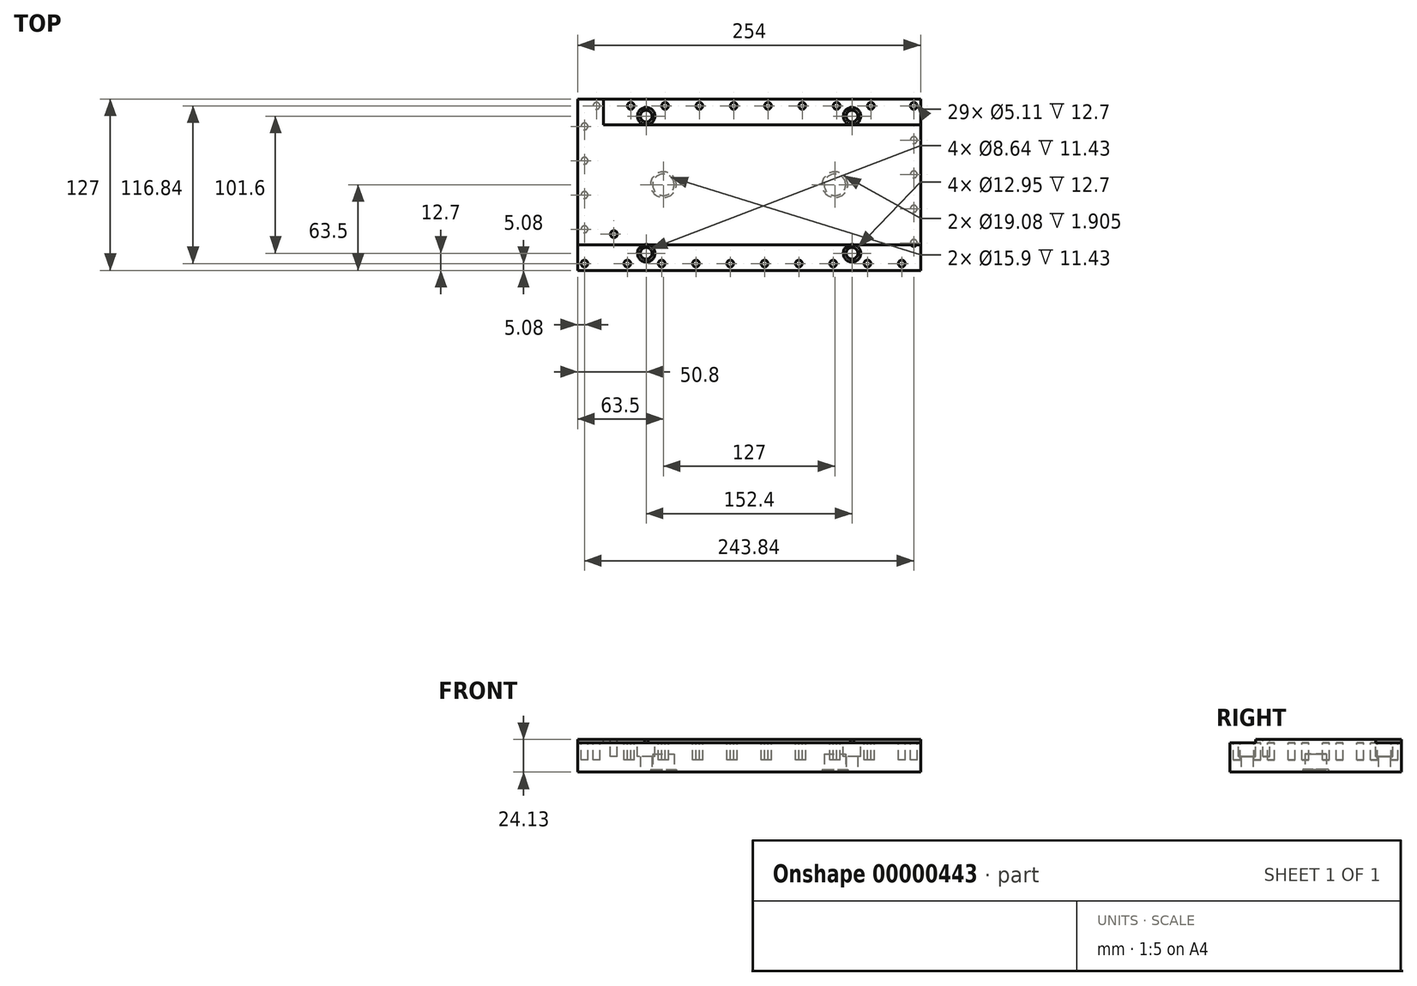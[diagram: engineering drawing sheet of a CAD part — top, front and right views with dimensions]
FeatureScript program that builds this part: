
annotation { "Feature Type Name" : "Feature", "Feature Type Description" : "" }
export const myFeature = defineFeature(function(context is Context, id is Id, definition is map)
    precondition{}
    {
        {
            var Q0;
            Q0=qCreatedBy(makeId("Top.planeOp"),FACE);
            var sketch = newSketch(context, id + "F0", { "sketchPlane" : qUnion([Q0])});
            skLineSegment(sketch, "E0.bottom", {"start": v(0, 0) * mm, "end": v(254, 0) * mm});
            skLineSegment(sketch, "E0.top", {"start": v(0, 127) * mm, "end": v(254, 127) * mm});
            skLineSegment(sketch, "E0.left", {"start": v(0, 0) * mm, "end": v(0, 127) * mm});
            skLineSegment(sketch, "E0.right", {"start": v(254, 0) * mm, "end": v(254, 127) * mm});
            skSolve(sketch);
        }
        {
            var Q0;
            Q0=makeQuery(id+"F0.imprint","IMPRINT",FACE,{"disambiguationData":[TD([[makeQuery(id+"F0.imprint","IMPRINT",EDGE,{"derivedFrom":sQuery(id+"F0.wireOp",EDGE,"E0.bottom")}),1.0]])]});
            extrude(context, id + "F1", {"entities" : qUnion([Q0]), "depth" : 24.13 * mm});
        }
        {
            var Q0;
            Q0=makeQuery(id+"F1.opExtrude","CAP_FACE",FACE,{"disambiguationData":[OSD([sQuery(id+"F0.wireOp",EDGE,"E0.bottom"),sQuery(id+"F0.wireOp",EDGE,"E0.top"),sQuery(id+"F0.wireOp",EDGE,"E0.left"),sQuery(id+"F0.wireOp",EDGE,"E0.right")])],"isStart":true});
            var sketch = newSketch(context, id + "F2", { "sketchPlane" : qUnion([Q0])});
            skCircle(sketch, "E1", {"center": v(190.5, -63.5) * mm, "radius": 7.95 * mm});
            skCircle(sketch, "E2", {"center": v(63.5, -63.5) * mm, "radius": 7.95 * mm});
            skSolve(sketch);
        }
        {
            var Q0;
            {Q0=qUnion([makeQuery(id+"F2.imprint","IMPRINT",FACE,{"disambiguationData":[TD([[makeQuery(id+"F2.imprint","IMPRINT",EDGE,{"derivedFrom":sQuery(id+"F2.wireOp",EDGE,"E1")}),1.0]])]}),makeQuery(id+"F2.imprint","IMPRINT",FACE,{"disambiguationData":[TD([[makeQuery(id+"F2.imprint","IMPRINT",EDGE,{"derivedFrom":sQuery(id+"F2.wireOp",EDGE,"E2")}),1.0]])]})]);}
            extrude(context, id + "F3", {"entities" : qUnion([Q0]), "operationType" : NewBodyOperationType.REMOVE, "oppositeDirection" : true, "depth" : 13.33 * mm});
        }
        {
            var Q0;
            Q0=makeQuery(id+"F1.opExtrude","CAP_FACE",FACE,{"disambiguationData":[OSD([sQuery(id+"F0.wireOp",EDGE,"E0.bottom"),sQuery(id+"F0.wireOp",EDGE,"E0.top"),sQuery(id+"F0.wireOp",EDGE,"E0.left"),sQuery(id+"F0.wireOp",EDGE,"E0.right")])],"isStart":true});
            var sketch = newSketch(context, id + "F4", { "sketchPlane" : qUnion([Q0])});
            skCircle(sketch, "E3", {"center": v(203.2, -114.3) * mm, "radius": 4.32 * mm});
            skCircle(sketch, "E4", {"center": v(203.2, -12.7) * mm, "radius": 4.32 * mm});
            skCircle(sketch, "E5", {"center": v(50.8, -114.3) * mm, "radius": 4.32 * mm});
            skCircle(sketch, "E6", {"center": v(50.8, -12.7) * mm, "radius": 4.32 * mm});
            skSolve(sketch);
        }
        {
            var Q0;
            {Q0=qUnion([makeQuery(id+"F4.imprint","IMPRINT",FACE,{"disambiguationData":[TD([[makeQuery(id+"F4.imprint","IMPRINT",EDGE,{"derivedFrom":sQuery(id+"F4.wireOp",EDGE,"E3")}),1.0]])]}),makeQuery(id+"F4.imprint","IMPRINT",FACE,{"disambiguationData":[TD([[makeQuery(id+"F4.imprint","IMPRINT",EDGE,{"derivedFrom":sQuery(id+"F4.wireOp",EDGE,"E4")}),1.0]])]}),makeQuery(id+"F4.imprint","IMPRINT",FACE,{"disambiguationData":[TD([[makeQuery(id+"F4.imprint","IMPRINT",EDGE,{"derivedFrom":sQuery(id+"F4.wireOp",EDGE,"E5")}),1.0]])]}),makeQuery(id+"F4.imprint","IMPRINT",FACE,{"disambiguationData":[TD([[makeQuery(id+"F4.imprint","IMPRINT",EDGE,{"derivedFrom":sQuery(id+"F4.wireOp",EDGE,"E6")}),1.0]])]})]);}
            extrude(context, id + "F5", {"entities" : qUnion([Q0]), "operationType" : NewBodyOperationType.REMOVE, "endBound" : BoundingType.THROUGH_ALL, "oppositeDirection" : true, "depth" : 25.4 * mm});
        }
        {
            var Q0;
            Q0=makeQuery(id+"F1.opExtrude","CAP_FACE",FACE,{"disambiguationData":[OSD([sQuery(id+"F0.wireOp",EDGE,"E0.bottom"),sQuery(id+"F0.wireOp",EDGE,"E0.top"),sQuery(id+"F0.wireOp",EDGE,"E0.left"),sQuery(id+"F0.wireOp",EDGE,"E0.right")])],"isStart":false});
            var sketch = newSketch(context, id + "F6", { "sketchPlane" : qUnion([Q0])});
            skCircle(sketch, "E7", {"center": v(50.8, 114.3) * mm, "radius": 6.48 * mm});
            skCircle(sketch, "E8", {"center": v(203.2, 114.3) * mm, "radius": 6.48 * mm});
            skCircle(sketch, "E9", {"center": v(50.8, 12.7) * mm, "radius": 6.48 * mm});
            skCircle(sketch, "E10", {"center": v(203.2, 12.7) * mm, "radius": 6.48 * mm});
            skSolve(sketch);
        }
        {
            var Q0;
            {var subQ0=makeQuery(id+"F1.opExtrude","CAP_FACE",FACE,{"disambiguationData":[OSD([sQuery(id+"F0.wireOp",EDGE,"E0.bottom"),sQuery(id+"F0.wireOp",EDGE,"E0.top"),sQuery(id+"F0.wireOp",EDGE,"E0.left"),sQuery(id+"F0.wireOp",EDGE,"E0.right")])],"isStart":false});var subQ1=makeQuery(id+"F6.imprint","IMPRINT",EDGE,{"derivedFrom":makeQuery(id+"F5.boolean.opBoolean","INTERSECT",EDGE,{"derivedFrom":[subQ0,makeQuery(id+"F5.opExtrude","SWEPT_FACE",FACE,{"disambiguationData":[OSD([sQuery(id+"F4.wireOp",EDGE,"E3")])]})]})});var subQ2=makeQuery(id+"F6.imprint","IMPRINT",EDGE,{"derivedFrom":makeQuery(id+"F5.boolean.opBoolean","INTERSECT",EDGE,{"derivedFrom":[subQ0,makeQuery(id+"F5.opExtrude","SWEPT_FACE",FACE,{"disambiguationData":[OSD([sQuery(id+"F4.wireOp",EDGE,"E4")])]})]})});var subQ3=makeQuery(id+"F6.imprint","IMPRINT",EDGE,{"derivedFrom":makeQuery(id+"F5.boolean.opBoolean","INTERSECT",EDGE,{"derivedFrom":[subQ0,makeQuery(id+"F5.opExtrude","SWEPT_FACE",FACE,{"disambiguationData":[OSD([sQuery(id+"F4.wireOp",EDGE,"E5")])]})]})});var subQ4=makeQuery(id+"F6.imprint","IMPRINT",EDGE,{"derivedFrom":makeQuery(id+"F5.boolean.opBoolean","INTERSECT",EDGE,{"derivedFrom":[subQ0,makeQuery(id+"F5.opExtrude","SWEPT_FACE",FACE,{"disambiguationData":[OSD([sQuery(id+"F4.wireOp",EDGE,"E6")])]})]})});Q0=qUnion([makeQuery(id+"F6.imprint","IMPRINT",FACE,{"disambiguationData":[TD([[subQ1,1.0]])]}),makeQuery(id+"F6.imprint","IMPRINT",FACE,{"disambiguationData":[TD([[subQ2,1.0]])]}),makeQuery(id+"F6.imprint","IMPRINT",FACE,{"disambiguationData":[TD([[subQ3,1.0]])]}),makeQuery(id+"F6.imprint","IMPRINT",FACE,{"disambiguationData":[TD([[subQ4,1.0]])]}),makeQuery(id+"F6.imprint","IMPRINT",FACE,{"disambiguationData":[TD([[makeQuery(id+"F6.imprint","IMPRINT",EDGE,{"derivedFrom":sQuery(id+"F6.wireOp",EDGE,"E7")}),1.0]])]}),makeQuery(id+"F6.imprint","IMPRINT",FACE,{"disambiguationData":[TD([[makeQuery(id+"F6.imprint","IMPRINT",EDGE,{"derivedFrom":sQuery(id+"F6.wireOp",EDGE,"E8")}),1.0]])]}),makeQuery(id+"F6.imprint","IMPRINT",FACE,{"disambiguationData":[TD([[makeQuery(id+"F6.imprint","IMPRINT",EDGE,{"derivedFrom":sQuery(id+"F6.wireOp",EDGE,"E9")}),1.0]])]}),makeQuery(id+"F6.imprint","IMPRINT",FACE,{"disambiguationData":[TD([[makeQuery(id+"F6.imprint","IMPRINT",EDGE,{"derivedFrom":sQuery(id+"F6.wireOp",EDGE,"E10")}),1.0]])]})]);}
            extrude(context, id + "F7", {"entities" : qUnion([Q0]), "operationType" : NewBodyOperationType.REMOVE, "oppositeDirection" : true, "depth" : 12.7 * mm});
        }
        {
            var Q0;
            Q0=makeQuery(id+"F1.opExtrude","CAP_FACE",FACE,{"disambiguationData":[OSD([sQuery(id+"F0.wireOp",EDGE,"E0.bottom"),sQuery(id+"F0.wireOp",EDGE,"E0.top"),sQuery(id+"F0.wireOp",EDGE,"E0.left"),sQuery(id+"F0.wireOp",EDGE,"E0.right")])],"isStart":false});
            var sketch = newSketch(context, id + "F8", { "sketchPlane" : qUnion([Q0])});
            skLineSegment(sketch, "E11.bottom", {"start": v(0, 19.05) * mm, "end": v(254, 19.05) * mm});
            skLineSegment(sketch, "E11.top", {"start": v(0, 0) * mm, "end": v(254, 0) * mm});
            skLineSegment(sketch, "E11.left", {"start": v(0, 19.05) * mm, "end": v(0, 0) * mm});
            skLineSegment(sketch, "E11.right", {"start": v(254, 19.05) * mm, "end": v(254, 0) * mm});
            skLineSegment(sketch, "E12.bottom", {"start": v(19.05, 19.05) * mm, "end": v(0, 19.05) * mm});
            skLineSegment(sketch, "E12.top", {"start": v(19.05, 127) * mm, "end": v(0, 127) * mm});
            skLineSegment(sketch, "E12.left", {"start": v(19.05, 19.05) * mm, "end": v(19.05, 127) * mm});
            skLineSegment(sketch, "E12.right", {"start": v(0, 19.05) * mm, "end": v(0, 127) * mm});
            skSolve(sketch);
        }
        {
            var Q0;
            {var subQ1=sQuery(id+"F8.wireOp",EDGE,"E12.bottom");var subQ2=makeQuery(id+"F8.imprint","IMPRINT",EDGE,{"derivedFrom":subQ1});var subQ3=makeQuery(id+"F7.boolean.opBoolean","COPY",EDGE,{"derivedFrom":makeQuery(id+"F7.opExtrude","CAP_EDGE",EDGE,{"disambiguationData":[OSD([sQuery(id+"F6.wireOp",EDGE,"E10")])],"isStart":true})});var subQ4=sQuery(id+"F8.wireOp",EDGE,"E11.bottom");var subQ6=makeQuery(id+"F8.imprint","INTERSECT",VERTEX,{"disambiguationData":[OD(0.0)],"derivedFrom":[subQ3,subQ4]});var subQ8=makeQuery(id+"F7.boolean.opBoolean","COPY",EDGE,{"derivedFrom":makeQuery(id+"F7.opExtrude","CAP_EDGE",EDGE,{"disambiguationData":[OSD([sQuery(id+"F6.wireOp",EDGE,"E9")])],"isStart":true})});var subQ10=makeQuery(id+"F8.imprint","INTERSECT",VERTEX,{"disambiguationData":[OD(0.0)],"derivedFrom":[subQ8,subQ4]});Q0=qUnion([makeQuery(id+"F8.imprint","IMPRINT",FACE,{"disambiguationData":[TD([[subQ2,-1.0]])]}),makeQuery(id+"F8.imprint","IMPRINT",FACE,{"disambiguationData":[TD([[makeQuery(id+"F8.imprint","IMPRINT",EDGE,{"derivedFrom":sQuery(id+"F8.wireOp",EDGE,"E11.top")}),1.0]])]}),makeQuery(id+"F8.imprint","IMPRINT",FACE,{"disambiguationData":[TD([[makeQuery(id+"F8.imprint","IMPRINT",EDGE,{"disambiguationData":[TD([[subQ10,-1.0]])],"derivedFrom":subQ4}),-1.0]])]}),makeQuery(id+"F8.imprint","IMPRINT",FACE,{"disambiguationData":[TD([[makeQuery(id+"F8.imprint","IMPRINT",EDGE,{"disambiguationData":[TD([[subQ6,-1.0]])],"derivedFrom":subQ4}),-1.0]])]})]);}
            extrude(context, id + "F9", {"entities" : qUnion([Q0]), "operationType" : NewBodyOperationType.REMOVE, "oppositeDirection" : true, "depth" : 2.54 * mm});
        }
        {
            var Q0;
            Q0=makeQuery(id+"F9.boolean.opBoolean","COPY",FACE,{"derivedFrom":makeQuery(id+"F9.opExtrude","CAP_FACE",FACE,{"disambiguationData":[OSD([sQuery(id+"F8.wireOp",EDGE,"E11.bottom"),sQuery(id+"F8.wireOp",EDGE,"E11.top"),sQuery(id+"F8.wireOp",EDGE,"E11.left"),sQuery(id+"F8.wireOp",EDGE,"E11.right"),sQuery(id+"F8.wireOp",EDGE,"E12.top"),sQuery(id+"F8.wireOp",EDGE,"E12.left"),sQuery(id+"F8.wireOp",EDGE,"E12.right")])],"isStart":false})});
            var sketch = newSketch(context, id + "F10", { "sketchPlane" : qUnion([Q0])});
            skCircle(sketch, "E13", {"center": v(5.08, 5.08) * mm, "radius": 2.55 * mm});
            skCircle(sketch, "E14", {"center": v(5.08, 30.48) * mm, "radius": 2.55 * mm});
            skCircle(sketch, "E15", {"center": v(5.08, 55.88) * mm, "radius": 2.55 * mm});
            skCircle(sketch, "E16", {"center": v(5.08, 81.28) * mm, "radius": 2.55 * mm});
            skCircle(sketch, "E17", {"center": v(36.83, 5.08) * mm, "radius": 2.55 * mm});
            skCircle(sketch, "E18", {"center": v(62.23, 5.08) * mm, "radius": 2.55 * mm});
            skCircle(sketch, "E19", {"center": v(87.63, 5.08) * mm, "radius": 2.55 * mm});
            skCircle(sketch, "E20", {"center": v(113.03, 5.08) * mm, "radius": 2.55 * mm});
            skCircle(sketch, "E21", {"center": v(138.43, 5.08) * mm, "radius": 2.55 * mm});
            skCircle(sketch, "E22", {"center": v(163.83, 5.08) * mm, "radius": 2.55 * mm});
            skCircle(sketch, "E23", {"center": v(189.23, 5.08) * mm, "radius": 2.55 * mm});
            skCircle(sketch, "E24", {"center": v(214.63, 5.08) * mm, "radius": 2.55 * mm});
            skCircle(sketch, "E25", {"center": v(5.08, 106.68) * mm, "radius": 2.55 * mm});
            skCircle(sketch, "E26", {"center": v(240.03, 5.08) * mm, "radius": 2.55 * mm});
            skSolve(sketch);
        }
        {
            var Q0;
            {Q0=qUnion([makeQuery(id+"F10.imprint","IMPRINT",FACE,{"disambiguationData":[TD([[makeQuery(id+"F10.imprint","IMPRINT",EDGE,{"derivedFrom":sQuery(id+"F10.wireOp",EDGE,"E13")}),1.0]])]}),makeQuery(id+"F10.imprint","IMPRINT",FACE,{"disambiguationData":[TD([[makeQuery(id+"F10.imprint","IMPRINT",EDGE,{"derivedFrom":sQuery(id+"F10.wireOp",EDGE,"E14")}),1.0]])]}),makeQuery(id+"F10.imprint","IMPRINT",FACE,{"disambiguationData":[TD([[makeQuery(id+"F10.imprint","IMPRINT",EDGE,{"derivedFrom":sQuery(id+"F10.wireOp",EDGE,"E15")}),1.0]])]}),makeQuery(id+"F10.imprint","IMPRINT",FACE,{"disambiguationData":[TD([[makeQuery(id+"F10.imprint","IMPRINT",EDGE,{"derivedFrom":sQuery(id+"F10.wireOp",EDGE,"E16")}),1.0]])]}),makeQuery(id+"F10.imprint","IMPRINT",FACE,{"disambiguationData":[TD([[makeQuery(id+"F10.imprint","IMPRINT",EDGE,{"derivedFrom":sQuery(id+"F10.wireOp",EDGE,"E17")}),1.0]])]}),makeQuery(id+"F10.imprint","IMPRINT",FACE,{"disambiguationData":[TD([[makeQuery(id+"F10.imprint","IMPRINT",EDGE,{"derivedFrom":sQuery(id+"F10.wireOp",EDGE,"E18")}),1.0]])]}),makeQuery(id+"F10.imprint","IMPRINT",FACE,{"disambiguationData":[TD([[makeQuery(id+"F10.imprint","IMPRINT",EDGE,{"derivedFrom":sQuery(id+"F10.wireOp",EDGE,"E19")}),1.0]])]}),makeQuery(id+"F10.imprint","IMPRINT",FACE,{"disambiguationData":[TD([[makeQuery(id+"F10.imprint","IMPRINT",EDGE,{"derivedFrom":sQuery(id+"F10.wireOp",EDGE,"E20")}),1.0]])]}),makeQuery(id+"F10.imprint","IMPRINT",FACE,{"disambiguationData":[TD([[makeQuery(id+"F10.imprint","IMPRINT",EDGE,{"derivedFrom":sQuery(id+"F10.wireOp",EDGE,"E21")}),1.0]])]}),makeQuery(id+"F10.imprint","IMPRINT",FACE,{"disambiguationData":[TD([[makeQuery(id+"F10.imprint","IMPRINT",EDGE,{"derivedFrom":sQuery(id+"F10.wireOp",EDGE,"E22")}),1.0]])]}),makeQuery(id+"F10.imprint","IMPRINT",FACE,{"disambiguationData":[TD([[makeQuery(id+"F10.imprint","IMPRINT",EDGE,{"derivedFrom":sQuery(id+"F10.wireOp",EDGE,"E23")}),1.0]])]}),makeQuery(id+"F10.imprint","IMPRINT",FACE,{"disambiguationData":[TD([[makeQuery(id+"F10.imprint","IMPRINT",EDGE,{"derivedFrom":sQuery(id+"F10.wireOp",EDGE,"E24")}),1.0]])]}),makeQuery(id+"F10.imprint","IMPRINT",FACE,{"disambiguationData":[TD([[makeQuery(id+"F10.imprint","IMPRINT",EDGE,{"derivedFrom":sQuery(id+"F10.wireOp",EDGE,"E25")}),1.0]])]}),makeQuery(id+"F10.imprint","IMPRINT",FACE,{"disambiguationData":[TD([[makeQuery(id+"F10.imprint","IMPRINT",EDGE,{"derivedFrom":sQuery(id+"F10.wireOp",EDGE,"E26")}),1.0]])]})]);}
            extrude(context, id + "F11", {"entities" : qUnion([Q0]), "operationType" : NewBodyOperationType.REMOVE, "oppositeDirection" : true, "depth" : 12.7 * mm});
        }
        {
            var Q0;
            Q0=makeQuery(id+"F1.opExtrude","CAP_FACE",FACE,{"disambiguationData":[OSD([sQuery(id+"F0.wireOp",EDGE,"E0.bottom"),sQuery(id+"F0.wireOp",EDGE,"E0.top"),sQuery(id+"F0.wireOp",EDGE,"E0.left"),sQuery(id+"F0.wireOp",EDGE,"E0.right")])],"isStart":false});
            var sketch = newSketch(context, id + "F12", { "sketchPlane" : qUnion([Q0])});
            skCircle(sketch, "E27", {"center": v(26.87, 26.87) * mm, "radius": 2.55 * mm});
            skSolve(sketch);
        }
        {
            var Q0;
            Q0=makeQuery(id+"F12.imprint","IMPRINT",FACE,{"disambiguationData":[TD([[makeQuery(id+"F12.imprint","IMPRINT",EDGE,{"derivedFrom":sQuery(id+"F12.wireOp",EDGE,"E27")}),1.0]])]});
            extrude(context, id + "F13", {"entities" : qUnion([Q0]), "operationType" : NewBodyOperationType.REMOVE, "oppositeDirection" : true, "depth" : 12.7 * mm});
        }
        {
            var Q0;
            Q0=makeQuery(id+"F1.opExtrude","CAP_FACE",FACE,{"disambiguationData":[OSD([sQuery(id+"F0.wireOp",EDGE,"E0.bottom"),sQuery(id+"F0.wireOp",EDGE,"E0.top"),sQuery(id+"F0.wireOp",EDGE,"E0.left"),sQuery(id+"F0.wireOp",EDGE,"E0.right")])],"isStart":false});
            var sketch = newSketch(context, id + "F14", { "sketchPlane" : qUnion([Q0])});
            skLineSegment(sketch, "E28.bottom", {"start": v(19.05, 127) * mm, "end": v(254, 127) * mm});
            skLineSegment(sketch, "E28.top", {"start": v(19.05, 107.95) * mm, "end": v(254, 107.95) * mm});
            skLineSegment(sketch, "E28.left", {"start": v(19.05, 127) * mm, "end": v(19.05, 107.95) * mm});
            skLineSegment(sketch, "E28.right", {"start": v(254, 127) * mm, "end": v(254, 107.95) * mm});
            skLineSegment(sketch, "E29.bottom", {"start": v(234.95, 107.95) * mm, "end": v(254, 107.95) * mm});
            skLineSegment(sketch, "E29.top", {"start": v(234.95, 19.05) * mm, "end": v(254, 19.05) * mm});
            skLineSegment(sketch, "E29.left", {"start": v(234.95, 107.95) * mm, "end": v(234.95, 19.05) * mm});
            skLineSegment(sketch, "E29.right", {"start": v(254, 107.95) * mm, "end": v(254, 19.05) * mm});
            skSolve(sketch);
        }
        {
            var Q0;
            {var subQ1=sQuery(id+"F14.wireOp",EDGE,"E29.bottom");var subQ2=makeQuery(id+"F14.imprint","IMPRINT",EDGE,{"derivedFrom":subQ1});var subQ3=makeQuery(id+"F7.boolean.opBoolean","COPY",EDGE,{"derivedFrom":makeQuery(id+"F7.opExtrude","CAP_EDGE",EDGE,{"disambiguationData":[OSD([sQuery(id+"F6.wireOp",EDGE,"E7")])],"isStart":true})});var subQ4=sQuery(id+"F14.wireOp",EDGE,"E28.top");var subQ6=makeQuery(id+"F14.imprint","INTERSECT",VERTEX,{"disambiguationData":[OD(0.0)],"derivedFrom":[subQ3,subQ4]});var subQ8=makeQuery(id+"F7.boolean.opBoolean","COPY",EDGE,{"derivedFrom":makeQuery(id+"F7.opExtrude","CAP_EDGE",EDGE,{"disambiguationData":[OSD([sQuery(id+"F6.wireOp",EDGE,"E8")])],"isStart":true})});var subQ10=makeQuery(id+"F14.imprint","INTERSECT",VERTEX,{"disambiguationData":[OD(0.0)],"derivedFrom":[subQ8,subQ4]});Q0=qUnion([makeQuery(id+"F14.imprint","IMPRINT",FACE,{"disambiguationData":[TD([[subQ2,-1.0]])]}),makeQuery(id+"F14.imprint","IMPRINT",FACE,{"disambiguationData":[TD([[makeQuery(id+"F14.imprint","IMPRINT",EDGE,{"derivedFrom":sQuery(id+"F14.wireOp",EDGE,"E28.bottom")}),-1.0]])]}),makeQuery(id+"F14.imprint","IMPRINT",FACE,{"disambiguationData":[TD([[makeQuery(id+"F14.imprint","IMPRINT",EDGE,{"disambiguationData":[TD([[subQ6,-1.0]])],"derivedFrom":subQ4}),1.0]])]}),makeQuery(id+"F14.imprint","IMPRINT",FACE,{"disambiguationData":[TD([[makeQuery(id+"F14.imprint","IMPRINT",EDGE,{"disambiguationData":[TD([[subQ10,-1.0]])],"derivedFrom":subQ4}),1.0]])]})]);}
            extrude(context, id + "F15", {"entities" : qUnion([Q0]), "operationType" : NewBodyOperationType.REMOVE, "oppositeDirection" : true, "depth" : 2.54 * mm});
        }
        {
            var Q0;
            Q0=makeQuery(id+"F15.boolean.opBoolean","MERGE",FACE,{"derivedFrom":[makeQuery(id+"F9.boolean.opBoolean","COPY",FACE,{"derivedFrom":makeQuery(id+"F9.opExtrude","CAP_FACE",FACE,{"disambiguationData":[OSD([sQuery(id+"F8.wireOp",EDGE,"E11.bottom"),sQuery(id+"F8.wireOp",EDGE,"E11.top"),sQuery(id+"F8.wireOp",EDGE,"E11.left"),sQuery(id+"F8.wireOp",EDGE,"E11.right"),sQuery(id+"F8.wireOp",EDGE,"E12.top"),sQuery(id+"F8.wireOp",EDGE,"E12.left"),sQuery(id+"F8.wireOp",EDGE,"E12.right")])],"isStart":false})}),makeQuery(id+"F15.opExtrude","CAP_FACE",FACE,{"disambiguationData":[OSD([sQuery(id+"F14.wireOp",EDGE,"E28.bottom"),sQuery(id+"F14.wireOp",EDGE,"E28.top"),sQuery(id+"F14.wireOp",EDGE,"E28.left"),sQuery(id+"F14.wireOp",EDGE,"E28.right"),sQuery(id+"F14.wireOp",EDGE,"E29.top"),sQuery(id+"F14.wireOp",EDGE,"E29.left"),sQuery(id+"F14.wireOp",EDGE,"E29.right")])],"isStart":false})]});
            var sketch = newSketch(context, id + "F16", { "sketchPlane" : qUnion([Q0])});
            skCircle(sketch, "E30", {"center": v(13.97, 121.92) * mm, "radius": 2.55 * mm});
            skCircle(sketch, "E31", {"center": v(39.37, 121.92) * mm, "radius": 2.55 * mm});
            skCircle(sketch, "E32", {"center": v(64.77, 121.92) * mm, "radius": 2.55 * mm});
            skCircle(sketch, "E33", {"center": v(90.17, 121.92) * mm, "radius": 2.55 * mm});
            skCircle(sketch, "E34", {"center": v(115.57, 121.92) * mm, "radius": 2.55 * mm});
            skCircle(sketch, "E35", {"center": v(140.97, 121.92) * mm, "radius": 2.55 * mm});
            skCircle(sketch, "E36", {"center": v(166.37, 121.92) * mm, "radius": 2.55 * mm});
            skCircle(sketch, "E37", {"center": v(191.77, 121.92) * mm, "radius": 2.55 * mm});
            skCircle(sketch, "E38", {"center": v(217.17, 121.92) * mm, "radius": 2.55 * mm});
            skCircle(sketch, "E39", {"center": v(248.92, 20.32) * mm, "radius": 2.55 * mm});
            skCircle(sketch, "E40", {"center": v(248.92, 45.72) * mm, "radius": 2.55 * mm});
            skCircle(sketch, "E41", {"center": v(248.92, 71.12) * mm, "radius": 2.55 * mm});
            skCircle(sketch, "E42", {"center": v(248.92, 96.52) * mm, "radius": 2.55 * mm});
            skCircle(sketch, "E43", {"center": v(248.92, 121.92) * mm, "radius": 2.55 * mm});
            skSolve(sketch);
        }
        {
            var Q0;
            {Q0=qUnion([makeQuery(id+"F16.imprint","IMPRINT",FACE,{"disambiguationData":[TD([[makeQuery(id+"F16.imprint","IMPRINT",EDGE,{"derivedFrom":sQuery(id+"F16.wireOp",EDGE,"E30")}),1.0]])]}),makeQuery(id+"F16.imprint","IMPRINT",FACE,{"disambiguationData":[TD([[makeQuery(id+"F16.imprint","IMPRINT",EDGE,{"derivedFrom":sQuery(id+"F16.wireOp",EDGE,"E31")}),1.0]])]}),makeQuery(id+"F16.imprint","IMPRINT",FACE,{"disambiguationData":[TD([[makeQuery(id+"F16.imprint","IMPRINT",EDGE,{"derivedFrom":sQuery(id+"F16.wireOp",EDGE,"E32")}),1.0]])]}),makeQuery(id+"F16.imprint","IMPRINT",FACE,{"disambiguationData":[TD([[makeQuery(id+"F16.imprint","IMPRINT",EDGE,{"derivedFrom":sQuery(id+"F16.wireOp",EDGE,"E33")}),1.0]])]}),makeQuery(id+"F16.imprint","IMPRINT",FACE,{"disambiguationData":[TD([[makeQuery(id+"F16.imprint","IMPRINT",EDGE,{"derivedFrom":sQuery(id+"F16.wireOp",EDGE,"E34")}),1.0]])]}),makeQuery(id+"F16.imprint","IMPRINT",FACE,{"disambiguationData":[TD([[makeQuery(id+"F16.imprint","IMPRINT",EDGE,{"derivedFrom":sQuery(id+"F16.wireOp",EDGE,"E35")}),1.0]])]}),makeQuery(id+"F16.imprint","IMPRINT",FACE,{"disambiguationData":[TD([[makeQuery(id+"F16.imprint","IMPRINT",EDGE,{"derivedFrom":sQuery(id+"F16.wireOp",EDGE,"E36")}),1.0]])]}),makeQuery(id+"F16.imprint","IMPRINT",FACE,{"disambiguationData":[TD([[makeQuery(id+"F16.imprint","IMPRINT",EDGE,{"derivedFrom":sQuery(id+"F16.wireOp",EDGE,"E37")}),1.0]])]}),makeQuery(id+"F16.imprint","IMPRINT",FACE,{"disambiguationData":[TD([[makeQuery(id+"F16.imprint","IMPRINT",EDGE,{"derivedFrom":sQuery(id+"F16.wireOp",EDGE,"E38")}),1.0]])]}),makeQuery(id+"F16.imprint","IMPRINT",FACE,{"disambiguationData":[TD([[makeQuery(id+"F16.imprint","IMPRINT",EDGE,{"derivedFrom":sQuery(id+"F16.wireOp",EDGE,"E39")}),1.0]])]}),makeQuery(id+"F16.imprint","IMPRINT",FACE,{"disambiguationData":[TD([[makeQuery(id+"F16.imprint","IMPRINT",EDGE,{"derivedFrom":sQuery(id+"F16.wireOp",EDGE,"E40")}),1.0]])]}),makeQuery(id+"F16.imprint","IMPRINT",FACE,{"disambiguationData":[TD([[makeQuery(id+"F16.imprint","IMPRINT",EDGE,{"derivedFrom":sQuery(id+"F16.wireOp",EDGE,"E41")}),1.0]])]}),makeQuery(id+"F16.imprint","IMPRINT",FACE,{"disambiguationData":[TD([[makeQuery(id+"F16.imprint","IMPRINT",EDGE,{"derivedFrom":sQuery(id+"F16.wireOp",EDGE,"E42")}),1.0]])]}),makeQuery(id+"F16.imprint","IMPRINT",FACE,{"disambiguationData":[TD([[makeQuery(id+"F16.imprint","IMPRINT",EDGE,{"derivedFrom":sQuery(id+"F16.wireOp",EDGE,"E43")}),1.0]])]})]);}
            extrude(context, id + "F17", {"entities" : qUnion([Q0]), "operationType" : NewBodyOperationType.REMOVE, "oppositeDirection" : true, "depth" : 12.7 * mm});
        }
        {
            var Q0;
            Q0=makeQuery(id+"F1.opExtrude","CAP_FACE",FACE,{"disambiguationData":[OSD([sQuery(id+"F0.wireOp",EDGE,"E0.bottom"),sQuery(id+"F0.wireOp",EDGE,"E0.top"),sQuery(id+"F0.wireOp",EDGE,"E0.left"),sQuery(id+"F0.wireOp",EDGE,"E0.right")])],"isStart":true});
            var sketch = newSketch(context, id + "F18", { "sketchPlane" : qUnion([Q0])});
            skCircle(sketch, "E44", {"center": v(63.5, -63.5) * mm, "radius": 9.54 * mm});
            skCircle(sketch, "E45", {"center": v(190.5, -63.5) * mm, "radius": 9.54 * mm});
            skSolve(sketch);
        }
        {
            var Q0;
            {var subQ0=makeQuery(id+"F18.imprint","IMPRINT",EDGE,{"derivedFrom":makeQuery(id+"F3.boolean.opBoolean","COPY",EDGE,{"derivedFrom":makeQuery(id+"F3.opExtrude","CAP_EDGE",EDGE,{"disambiguationData":[OSD([sQuery(id+"F2.wireOp",EDGE,"E1")])],"isStart":true})})});var subQ1=makeQuery(id+"F18.imprint","IMPRINT",EDGE,{"derivedFrom":makeQuery(id+"F3.boolean.opBoolean","COPY",EDGE,{"derivedFrom":makeQuery(id+"F3.opExtrude","CAP_EDGE",EDGE,{"disambiguationData":[OSD([sQuery(id+"F2.wireOp",EDGE,"E2")])],"isStart":true})})});Q0=qUnion([makeQuery(id+"F18.imprint","IMPRINT",FACE,{"disambiguationData":[TD([[subQ0,1.0]])]}),makeQuery(id+"F18.imprint","IMPRINT",FACE,{"disambiguationData":[TD([[subQ1,1.0]])]}),makeQuery(id+"F18.imprint","IMPRINT",FACE,{"disambiguationData":[TD([[makeQuery(id+"F18.imprint","IMPRINT",EDGE,{"derivedFrom":sQuery(id+"F18.wireOp",EDGE,"E44")}),1.0]])]}),makeQuery(id+"F18.imprint","IMPRINT",FACE,{"disambiguationData":[TD([[makeQuery(id+"F18.imprint","IMPRINT",EDGE,{"derivedFrom":sQuery(id+"F18.wireOp",EDGE,"E45")}),1.0]])]})]);}
            extrude(context, id + "F19", {"entities" : qUnion([Q0]), "operationType" : NewBodyOperationType.REMOVE, "oppositeDirection" : true, "depth" : 1.9 * mm});
        }
    });
